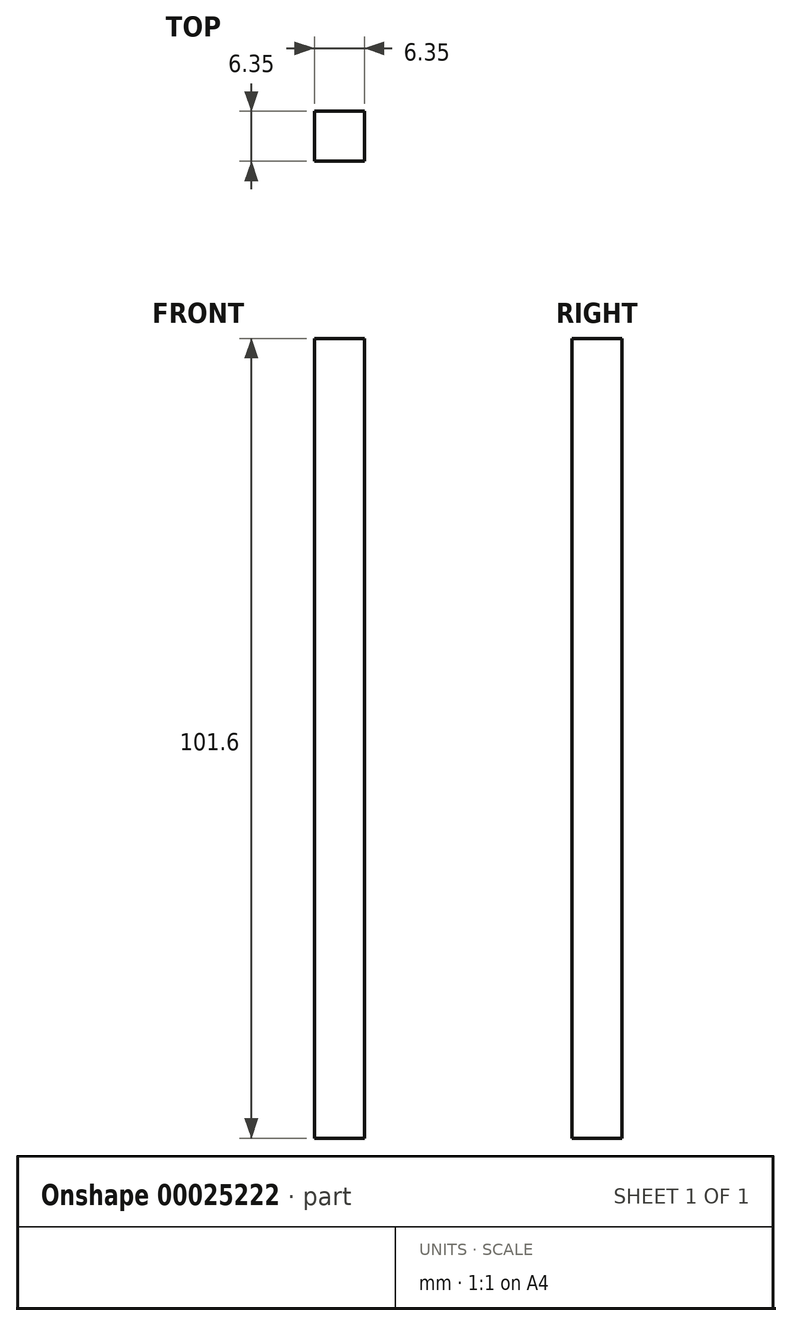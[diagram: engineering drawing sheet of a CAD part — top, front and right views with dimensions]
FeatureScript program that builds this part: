
annotation { "Feature Type Name" : "Feature", "Feature Type Description" : "" }
export const myFeature = defineFeature(function(context is Context, id is Id, definition is map)
    precondition{}
    {
        {
            var Q0;
            Q0=qCreatedBy(makeId("Front.planeOp"),FACE);
            var sketch = newSketch(context, id + "F0", { "sketchPlane" : qUnion([Q0])});
            skLineSegment(sketch, "E0", {"start": v(0, 0) * mm, "end": v(0, 101.6) * mm});
            skLineSegment(sketch, "E1", {"start": v(0, 0) * mm, "end": v(6.35, 0) * mm});
            skLineSegment(sketch, "E2", {"start": v(6.35, 0) * mm, "end": v(6.35, 101.6) * mm});
            skLineSegment(sketch, "E3", {"start": v(0, 101.6) * mm, "end": v(6.35, 101.6) * mm});
            skSolve(sketch);
        }
        {
            var Q0;
            Q0 = qSketchRegion(id + "F0", true);
            extrude(context, id + "F1", {"entities" : qUnion([Q0]), "depth" : 6.35 * mm});
        }
    });
